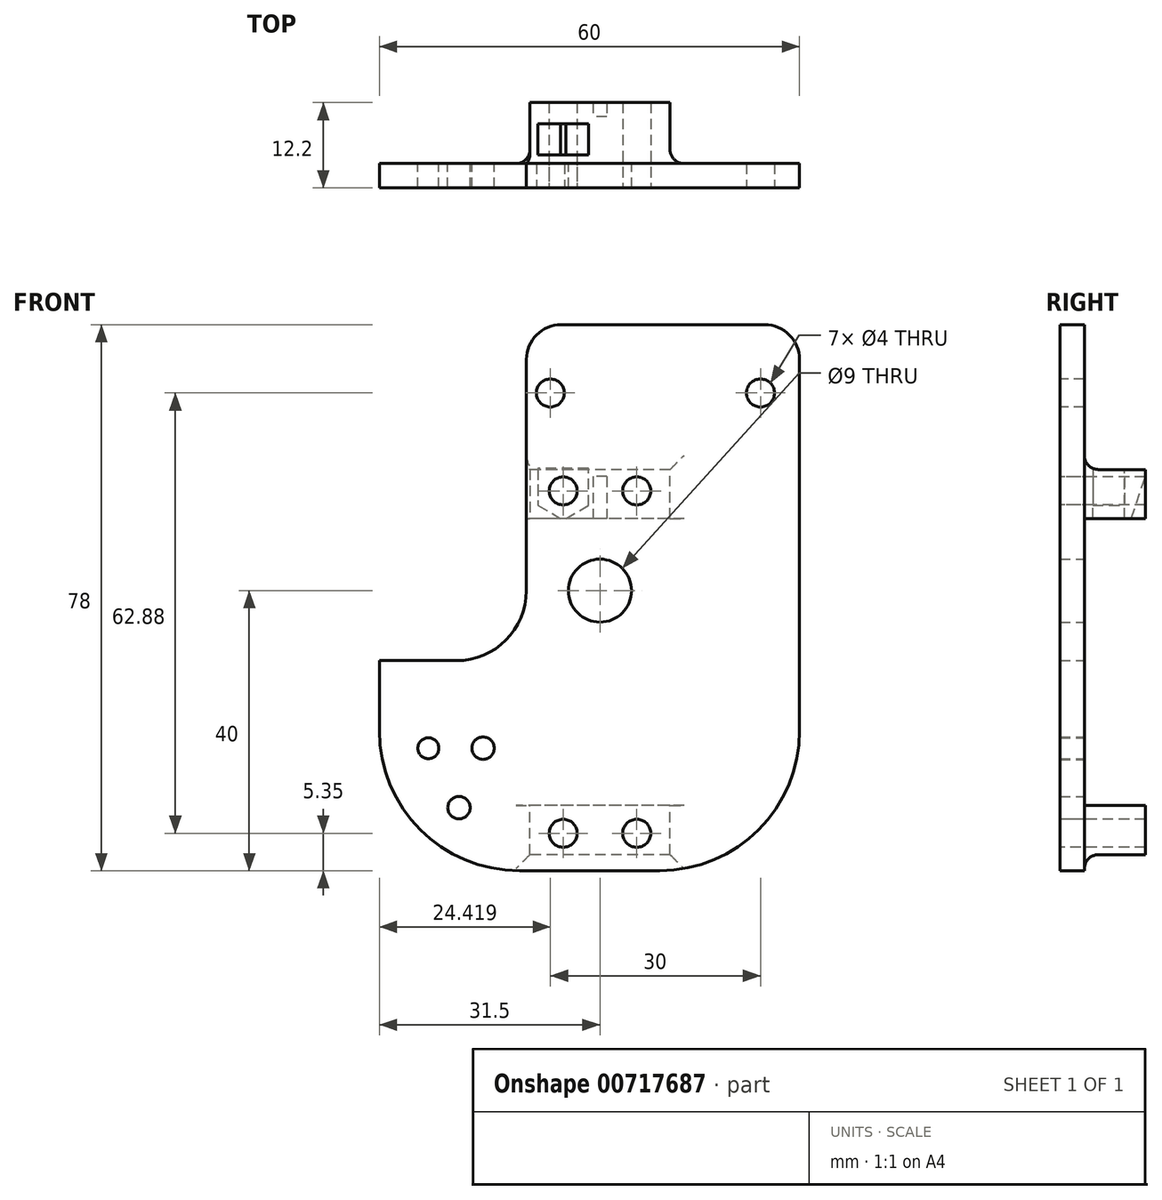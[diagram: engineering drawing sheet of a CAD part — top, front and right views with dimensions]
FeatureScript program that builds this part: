
annotation { "Feature Type Name" : "Feature", "Feature Type Description" : "" }
export const myFeature = defineFeature(function(context is Context, id is Id, definition is map)
    precondition{}
    {
        {
            var Q0;
            Q0=qCreatedBy(makeId("Front.planeOp"),FACE);
            var sketch = newSketch(context, id + "F0", { "sketchPlane" : qUnion([Q0])});
            skPoint(sketch, "E0.middle", {"position": v(0, 0) * mm});
            skLineSegment(sketch, "E1.bottom", {"start": v(-21.91, -4.91) * mm, "end": v(0.79, 17.64) * mm, "construction": true});
            skLineSegment(sketch, "E1.top", {"start": v(-25.44, -1.36) * mm, "end": v(-2.73, 21.19) * mm, "construction": true});
            skPoint(sketch, "E1.middle", {"position": v(-12.32, 8.14) * mm});
            skArc(sketch, "E2", {"start": v(-25.44, -1.36) * mm, "mid": v(-25.45, -4.9) * mm, "end": v(-21.91, -4.91) * mm, "construction": true});
            skArc(sketch, "E3", {"start": v(0.79, 17.64) * mm, "mid": v(0.8, 21.17) * mm, "end": v(-2.73, 21.19) * mm, "construction": true});
            skCircle(sketch, "E4", {"center": v(-18, 2.5) * mm, "radius": 1.5 * mm});
            skCircle(sketch, "E5", {"center": v(-10.2, 2.5) * mm, "radius": 2.5 * mm, "construction": true});
            skLineSegment(sketch, "E6", {"start": v(-21.58, -5.08) * mm, "end": v(-17.16, 26.62) * mm, "construction": true});
            skLineSegment(sketch, "E7", {"start": v(-16.63, -5.77) * mm, "end": v(-12.21, 25.92) * mm, "construction": true});
            skArc(sketch, "E8", {"start": v(-21.58, -5.08) * mm, "mid": v(-19.45, -7.9) * mm, "end": v(-16.63, -5.77) * mm, "construction": true});
            skArc(sketch, "E9", {"start": v(-12.21, 25.92) * mm, "mid": v(-14.34, 28.75) * mm, "end": v(-17.16, 26.62) * mm, "construction": true});
            skLineSegment(sketch, "E10", {"start": v(-1.22, 10.2) * mm, "end": v(9.5, 41.42) * mm, "construction": true});
            skLineSegment(sketch, "E11", {"start": v(3.5, 8.58) * mm, "end": v(14.22, 39.8) * mm, "construction": true});
            skArc(sketch, "E12", {"start": v(-1.22, 10.2) * mm, "mid": v(0.33, 7.03) * mm, "end": v(3.5, 8.58) * mm, "construction": true});
            skArc(sketch, "E13", {"start": v(14.22, 39.8) * mm, "mid": v(12.67, 42.97) * mm, "end": v(9.5, 41.42) * mm, "construction": true});
            skLineSegment(sketch, "E14", {"start": v(-19.1, -5.42) * mm, "end": v(-14.69, 26.27) * mm, "construction": true});
            skLineSegment(sketch, "E15", {"start": v(1.14, 9.4) * mm, "end": v(11.86, 40.6) * mm, "construction": true});
            skPoint(sketch, "E16", {"position": v(6.5, 25) * mm});
            skLineSegment(sketch, "E17", {"start": v(23.11, 23.42) * mm, "end": v(-9.84, 21.59) * mm, "construction": true});
            skLineSegment(sketch, "E18", {"start": v(22.84, 28.41) * mm, "end": v(-10.11, 26.58) * mm, "construction": true});
            skArc(sketch, "E19", {"start": v(23.11, 23.42) * mm, "mid": v(25.47, 26.06) * mm, "end": v(22.84, 28.41) * mm, "construction": true});
            skArc(sketch, "E20", {"start": v(-10.11, 26.58) * mm, "mid": v(-12.47, 23.94) * mm, "end": v(-9.84, 21.59) * mm, "construction": true});
            skLineSegment(sketch, "E21", {"start": v(22.97, 25.92) * mm, "end": v(-9.97, 24.08) * mm, "construction": true});
            skPoint(sketch, "E22", {"position": v(-16.9, 10.42) * mm});
            skCircle(sketch, "E23", {"center": v(6.5, 25) * mm, "radius": 4.5 * mm});
            skLineSegment(sketch, "E24.bottom", {"start": v(-25, 45) * mm, "end": v(35, 45) * mm});
            skLineSegment(sketch, "E24.top", {"start": v(-25, -15) * mm, "end": v(35, -15) * mm});
            skLineSegment(sketch, "E24.left", {"start": v(-25, 45) * mm, "end": v(-25, -15) * mm});
            skLineSegment(sketch, "E24.right", {"start": v(35, 45) * mm, "end": v(35, -15) * mm});
            skCircle(sketch, "E25", {"center": v(6.5, 25) * mm, "radius": 6 * mm, "construction": true});
            skLineSegment(sketch, "E26", {"start": v(-23.68, -3.14) * mm, "end": v(-0.97, 19.41) * mm, "construction": true});
            skCircle(sketch, "E27", {"center": v(-18, 2.5) * mm, "radius": 10.5 * mm, "construction": true});
            skPoint(sketch, "E28", {"position": v(-25.45, -4.9) * mm});
            skPoint(sketch, "E29", {"position": v(-19.45, -7.9) * mm});
            skCircle(sketch, "E30", {"center": v(-13.63, -6) * mm, "radius": 2.5 * mm, "construction": true});
            skSolve(sketch);
        }
        {
            var Q0;
            Q0=makeQuery(id+"F0.imprint","IMPRINT",FACE,{"disambiguationData":[TD([[makeQuery(id+"F0.imprint","IMPRINT",EDGE,{"derivedFrom":sQuery(id+"F0.wireOp",EDGE,"E4")}),-1.0]])]});
            extrude(context, id + "F1", {"entities" : qUnion([Q0]), "depth" : 3.5 * mm, "offsetDistance" : 25 * mm});
        }
        {
            var Q0;
            Q0=makeQuery(id+"F1.opExtrude","CAP_FACE",FACE,{"disambiguationData":[OSD([sQuery(id+"F0.wireOp",EDGE,"E4"),sQuery(id+"F0.wireOp",EDGE,"E23"),sQuery(id+"F0.wireOp",EDGE,"E24.bottom"),sQuery(id+"F0.wireOp",EDGE,"E24.top"),sQuery(id+"F0.wireOp",EDGE,"E24.left"),sQuery(id+"F0.wireOp",EDGE,"E24.right")])],"isStart":false});
            var sketch = newSketch(context, id + "F2", { "sketchPlane" : qUnion([Q0])});
            skLineSegment(sketch, "E31.bottom", {"start": v(11.75, -9.65) * mm, "end": v(1.25, -9.65) * mm, "construction": true});
            skLineSegment(sketch, "E31.top", {"start": v(11.75, 39.25) * mm, "end": v(1.25, 39.25) * mm, "construction": true});
            skLineSegment(sketch, "E31.left", {"start": v(11.75, -9.65) * mm, "end": v(11.75, 39.25) * mm, "construction": true});
            skLineSegment(sketch, "E31.right", {"start": v(1.25, -9.65) * mm, "end": v(1.25, 39.25) * mm, "construction": true});
            skPoint(sketch, "E31.middle", {"position": v(6.5, 14.8) * mm});
            skLineSegment(sketch, "E32.bottom", {"start": v(16.5, 35.3) * mm, "end": v(-3.5, 35.3) * mm});
            skLineSegment(sketch, "E32.top", {"start": v(16.5, 42.3) * mm, "end": v(-3.5, 42.3) * mm});
            skLineSegment(sketch, "E32.left", {"start": v(16.5, 35.3) * mm, "end": v(16.5, 42.3) * mm});
            skLineSegment(sketch, "E32.right", {"start": v(-3.5, 35.3) * mm, "end": v(-3.5, 42.3) * mm});
            skPoint(sketch, "E32.middle", {"position": v(6.5, 38.8) * mm});
            skLineSegment(sketch, "E33.bottom", {"start": v(16.5, -12.7) * mm, "end": v(-3.5, -12.7) * mm});
            skLineSegment(sketch, "E33.top", {"start": v(16.5, -5.7) * mm, "end": v(-3.5, -5.7) * mm});
            skLineSegment(sketch, "E33.left", {"start": v(16.5, -12.7) * mm, "end": v(16.5, -5.7) * mm});
            skLineSegment(sketch, "E33.right", {"start": v(-3.5, -12.7) * mm, "end": v(-3.5, -5.7) * mm});
            skPoint(sketch, "E33.middle", {"position": v(6.5, -9.2) * mm});
            skLineSegment(sketch, "E34", {"start": v(11.75, 14.8) * mm, "end": v(1.25, 14.8) * mm, "construction": true});
            skLineSegment(sketch, "E35", {"start": v(6.5, 39.25) * mm, "end": v(6.5, -9.65) * mm, "construction": true});
            skSolve(sketch);
        }
        {
            var Q0;
            Q0 = qSketchRegion(id + "F2", true);
            extrude(context, id + "F3", {"entities" : qUnion([Q0]), "operationType" : NewBodyOperationType.ADD, "oppositeDirection" : true, "depth" : 12.2 * mm, "offsetDistance" : 25 * mm});
        }
        {
            var Q0;
            Q0=sQuery(id+"F2.wireOp",VERTEX,"E31.left.end");
            var Q1;
            Q1=sQuery(id+"F2.wireOp",VERTEX,"E31.top.end");
            var Q2;
            Q2=sQuery(id+"F2.wireOp",VERTEX,"E31.left.start");
            var Q3;
            Q3=sQuery(id+"F2.wireOp",VERTEX,"E31.right.start");
            var Q4;
            Q4=makeQuery(id+"F1.opExtrude","SWEPT_BODY",BODY,{"disambiguationData":[OSD([sQuery(id+"F0.wireOp",EDGE,"E4"),sQuery(id+"F0.wireOp",EDGE,"E23"),sQuery(id+"F0.wireOp",EDGE,"E24.bottom"),sQuery(id+"F0.wireOp",EDGE,"E24.top"),sQuery(id+"F0.wireOp",EDGE,"E24.left"),sQuery(id+"F0.wireOp",EDGE,"E24.right")])]});
            hole(context, id + "F4", {"style" : HoleStyle.SIMPLE, "endStyle" : HoleEndStyle.THROUGH, "holeDiameter" : 4 * mm, "majorDiameter" : 5 * mm, "isTappedThrough" : true, "tappedDepth" : 2.3 * mm, "tapClearance" : 3, "startFromSketch" : true, "locations" : qUnion([Q0, Q1, Q2, Q3]), "scope" : qUnion([Q4])});
        }
        {
            var Q0;
            Q0=makeQuery(id+"F3.opExtrude","CAP_FACE",FACE,{"disambiguationData":[OSD([sQuery(id+"F2.wireOp",EDGE,"E32.bottom"),sQuery(id+"F2.wireOp",EDGE,"E32.top"),sQuery(id+"F2.wireOp",EDGE,"E32.left"),sQuery(id+"F2.wireOp",EDGE,"E32.right")])],"isStart":false});
            cPlane(context, id + "F5", {"entities" : qUnion([Q0]), "cplaneType" : CPlaneType.OFFSET, "offset" : 3 * mm, "oppositeDirection" : true, "width" : 150 * mm, "height" : 150 * mm});
        }
        {
            var Q0;
            Q0=sQuery(id+"F2.wireOp",EDGE,"E35");
            cPoint(context, id + "F6", {"entities" : qUnion([Q0]), "parameter" : 0.5});
        }
        {
            var Q0;
            Q0=qCreatedBy(makeId("Top.planeOp"),FACE);
            var Q1;
            Q1 = qCreatedBy(id + "F6" ,VERTEX);
            cPlane(context, id + "F7", {"entities" : qUnion([Q0, Q1]), "cplaneType" : CPlaneType.PLANE_POINT, "offset" : 25 * mm, "width" : 150 * mm, "height" : 150 * mm});
        }
        {
            var Q0;
            Q0=qCreatedBy(makeId("Right.planeOp"),FACE);
            var Q1;
            Q1=sQuery(id+"F0.wireOp",VERTEX,"E16");
            cPlane(context, id + "F8", {"entities" : qUnion([Q0, Q1]), "cplaneType" : CPlaneType.PLANE_POINT, "offset" : 25 * mm, "width" : 150 * mm, "height" : 150 * mm});
        }
        {
            var Q0;
            Q0=qCreatedBy(id+"F5.planeOp",FACE);
            var sketch = newSketch(context, id + "F9", { "sketchPlane" : qUnion([Q0])});
            skCircle(sketch, "E36.cCircle", {"center": v(-1.25, 39.25) * mm, "radius": 3.6 * mm, "construction": true});
            skLineSegment(sketch, "E36.0", {"start": v(2.35, 37.17) * mm, "end": v(-1.25, 35.1) * mm});
            skLineSegment(sketch, "E36.1", {"start": v(-1.25, 35.1) * mm, "end": v(-4.85, 37.17) * mm});
            skLineSegment(sketch, "E36.2", {"start": v(-4.85, 37.17) * mm, "end": v(-4.85, 41.33) * mm});
            skLineSegment(sketch, "E36.3", {"start": v(-4.85, 41.33) * mm, "end": v(-1.25, 43.4) * mm});
            skLineSegment(sketch, "E36.4", {"start": v(-1.25, 43.4) * mm, "end": v(2.35, 41.33) * mm});
            skLineSegment(sketch, "E36.5", {"start": v(2.35, 41.33) * mm, "end": v(2.35, 37.17) * mm});
            skPoint(sketch, "E36.0.midPoint", {"position": v(0.55, 36.13) * mm});
            skLineSegment(sketch, "E37", {"start": v(-4.85, 41.33) * mm, "end": v(-4.85, 42.3) * mm});
            skLineSegment(sketch, "E38", {"start": v(-4.85, 42.3) * mm, "end": v(2.35, 42.3) * mm});
            skLineSegment(sketch, "E39", {"start": v(2.35, 42.3) * mm, "end": v(2.35, 41.33) * mm});
            skSolve(sketch);
        }
        {
            var Q0;
            Q0 = qSketchRegion(id + "F9", true);
            extrude(context, id + "F10", {"entities" : qUnion([Q0]), "operationType" : NewBodyOperationType.REMOVE, "oppositeDirection" : true, "depth" : 4.5 * mm, "offsetDistance" : 25 * mm});
        }
        {
            var Q0;
            Q0=qCreatedBy(makeId("Front.planeOp"),FACE);
            var sketch = newSketch(context, id + "F11", { "sketchPlane" : qUnion([Q0])});
            skLineSegment(sketch, "E40.bottom", {"start": v(35, 45) * mm, "end": v(-4, 45) * mm});
            skLineSegment(sketch, "E40.top", {"start": v(35, 63) * mm, "end": v(-4, 63) * mm});
            skLineSegment(sketch, "E40.left", {"start": v(35, 45) * mm, "end": v(35, 63) * mm});
            skLineSegment(sketch, "E40.right", {"start": v(-4, 45) * mm, "end": v(-4, 63) * mm});
            skSolve(sketch);
        }
        {
            var Q0;
            Q0=makeQuery(id+"F11.imprint","IMPRINT",FACE,{"disambiguationData":[TD([[makeQuery(id+"F11.imprint","IMPRINT",EDGE,{"derivedFrom":sQuery(id+"F11.wireOp",EDGE,"E40.bottom")}),-1.0]])]});
            var Q1;
            Q1=makeQuery(id+"F1.opExtrude","CAP_FACE",FACE,{"disambiguationData":[OSD([sQuery(id+"F0.wireOp",EDGE,"E4"),sQuery(id+"F0.wireOp",EDGE,"E23"),sQuery(id+"F0.wireOp",EDGE,"E24.bottom"),sQuery(id+"F0.wireOp",EDGE,"E24.top"),sQuery(id+"F0.wireOp",EDGE,"E24.left"),sQuery(id+"F0.wireOp",EDGE,"E24.right")])],"isStart":false});
            extrude(context, id + "F12", {"entities" : qUnion([Q0]), "operationType" : NewBodyOperationType.ADD, "endBound" : BoundingType.UP_TO_SURFACE, "depth" : 25 * mm, "endBoundEntityFace" : qUnion([Q1]), "offsetDistance" : 25 * mm});
        }
        {
            var Q0;
            Q0=makeQuery(id+"F2.imprint","IMPRINT",FACE,{"disambiguationData":[TD([[makeQuery(id+"F2.imprint","IMPRINT",EDGE,{"derivedFrom":sQuery(id+"F2.wireOp",EDGE,"E32.bottom")}),1.0]])]});
            var sketch = newSketch(context, id + "F13", { "sketchPlane" : qUnion([Q0])});
            skPoint(sketch, "E41", {"position": v(-0.58, 53.23) * mm});
            skPoint(sketch, "E42", {"position": v(29.42, 53.23) * mm});
            skLineSegment(sketch, "E43", {"start": v(-32.58, 62.23) * mm, "end": v(-32.58, -14.27) * mm, "construction": true});
            skLineSegment(sketch, "E44", {"start": v(-32.58, -9.27) * mm, "end": v(-22.58, -9.27) * mm, "construction": true});
            skCircle(sketch, "E45", {"center": v(-25.58, -9.27) * mm, "radius": 3 * mm, "construction": true});
            skLineSegment(sketch, "E46", {"start": v(-95.3, 32.33) * mm, "end": v(-95.3, -44.17) * mm, "construction": true});
            skLineSegment(sketch, "E47", {"start": v(-95.3, -39.17) * mm, "end": v(-85.3, -39.17) * mm, "construction": true});
            skLineSegment(sketch, "E48", {"start": v(-151.09, 43.62) * mm, "end": v(-151.09, -32.88) * mm, "construction": true});
            skLineSegment(sketch, "E49", {"start": v(-151.09, -27.88) * mm, "end": v(-141.09, -27.88) * mm, "construction": true});
            skLineSegment(sketch, "E50", {"start": v(-178.62, 52.62) * mm, "end": v(-178.62, -23.88) * mm, "construction": true});
            skLineSegment(sketch, "E51", {"start": v(-178.62, -18.88) * mm, "end": v(-168.62, -18.88) * mm, "construction": true});
            skSolve(sketch);
        }
        {
            var Q0;
            Q0=sQuery(id+"F13.wireOp",VERTEX,"E41");
            var Q1;
            Q1=sQuery(id+"F13.wireOp",VERTEX,"E42");
            var Q2;
            Q2=makeQuery(id+"F1.opExtrude","SWEPT_BODY",BODY,{"disambiguationData":[OSD([sQuery(id+"F0.wireOp",EDGE,"E4"),sQuery(id+"F0.wireOp",EDGE,"E23"),sQuery(id+"F0.wireOp",EDGE,"E24.bottom"),sQuery(id+"F0.wireOp",EDGE,"E24.top"),sQuery(id+"F0.wireOp",EDGE,"E24.left"),sQuery(id+"F0.wireOp",EDGE,"E24.right")])]});
            hole(context, id + "F14", {"style" : HoleStyle.SIMPLE, "endStyle" : HoleEndStyle.THROUGH, "holeDiameter" : 4 * mm, "majorDiameter" : 5 * mm, "isTappedThrough" : true, "tappedDepth" : 2.3 * mm, "tapClearance" : 3, "startFromSketch" : true, "locations" : qUnion([Q0, Q1]), "scope" : qUnion([Q2])});
        }
        {
            var Q0;
            Q0=sQuery(id+"F0.wireOp",VERTEX,"E5.center");
            var Q1;
            Q1=sQuery(id+"F0.wireOp",VERTEX,"E30.center");
            var Q2;
            Q2=makeQuery(id+"F1.opExtrude","SWEPT_BODY",BODY,{"disambiguationData":[OSD([sQuery(id+"F0.wireOp",EDGE,"E4"),sQuery(id+"F0.wireOp",EDGE,"E23"),sQuery(id+"F0.wireOp",EDGE,"E24.bottom"),sQuery(id+"F0.wireOp",EDGE,"E24.top"),sQuery(id+"F0.wireOp",EDGE,"E24.left"),sQuery(id+"F0.wireOp",EDGE,"E24.right")])]});
            hole(context, id + "F15", {"style" : HoleStyle.SIMPLE, "endStyle" : HoleEndStyle.THROUGH, "oppositeDirection" : true, "holeDiameter" : 3.2 * mm, "majorDiameter" : 5 * mm, "isTappedThrough" : true, "tappedDepth" : 2.3 * mm, "tapClearance" : 3, "startFromSketch" : true, "locations" : qUnion([Q0, Q1]), "scope" : qUnion([Q2])});
        }
        {
            var Q0;
            Q0=qCreatedBy(makeId("Front.planeOp"),FACE);
            var sketch = newSketch(context, id + "F16", { "sketchPlane" : qUnion([Q0])});
            skLineSegment(sketch, "E52.bottom", {"start": v(-25, 45) * mm, "end": v(-4, 45) * mm});
            skLineSegment(sketch, "E52.top", {"start": v(-25, 15) * mm, "end": v(-4, 15) * mm});
            skLineSegment(sketch, "E52.left", {"start": v(-25, 45) * mm, "end": v(-25, 15) * mm});
            skLineSegment(sketch, "E52.right", {"start": v(-4, 45) * mm, "end": v(-4, 15) * mm});
            skSolve(sketch);
        }
        {
            var Q0;
            Q0=makeQuery(id+"F16.imprint","IMPRINT",FACE,{"disambiguationData":[TD([[makeQuery(id+"F16.imprint","IMPRINT",EDGE,{"derivedFrom":sQuery(id+"F16.wireOp",EDGE,"E52.bottom")}),-1.0]])]});
            extrude(context, id + "F17", {"entities" : qUnion([Q0]), "operationType" : NewBodyOperationType.REMOVE, "depth" : 25 * mm, "offsetDistance" : 25 * mm});
        }
        {
            var Q0;
            Q0=makeQuery(id+"F1.opExtrude","SWEPT_EDGE",EDGE,{"disambiguationData":[OSD([sQuery(id+"F0.wireOp",EDGE,"E24.top"),sQuery(id+"F0.wireOp",EDGE,"E24.right")])]});
            var Q1;
            Q1=makeQuery(id+"F1.opExtrude","SWEPT_EDGE",EDGE,{"disambiguationData":[OSD([sQuery(id+"F0.wireOp",EDGE,"E24.top"),sQuery(id+"F0.wireOp",EDGE,"E24.left")])]});
            fillet(context, id + "F18", {"entities" : qUnion([Q0, Q1]), "radius" : 20 * mm, "tangentPropagation" : true, "allowEdgeOverflow" : false});
        }
        {
            var Q0;
            Q0=makeQuery(id+"F12.opExtrude","SWEPT_EDGE",EDGE,{"disambiguationData":[OSD([sQuery(id+"F11.wireOp",EDGE,"E40.bottom"),sQuery(id+"F11.wireOp",EDGE,"E40.right")])]});
            var Q1;
            Q1=makeQuery(id+"F12.opExtrude","SWEPT_EDGE",EDGE,{"disambiguationData":[OSD([sQuery(id+"F11.wireOp",EDGE,"E40.top"),sQuery(id+"F11.wireOp",EDGE,"E40.right")])]});
            var Q2;
            Q2=makeQuery(id+"F12.opExtrude","SWEPT_EDGE",EDGE,{"disambiguationData":[OSD([sQuery(id+"F11.wireOp",EDGE,"E40.top"),sQuery(id+"F11.wireOp",EDGE,"E40.left")])]});
            fillet(context, id + "F19", {"entities" : qUnion([Q0, Q1, Q2]), "radius" : 5 * mm, "tangentPropagation" : true, "allowEdgeOverflow" : false});
        }
        {
            var Q0;
            Q0=makeQuery(id+"F17.boolean.opBoolean","COPY",EDGE,{"derivedFrom":makeQuery(id+"F17.opExtrude","SWEPT_EDGE",EDGE,{"disambiguationData":[OSD([sQuery(id+"F16.wireOp",EDGE,"E52.top"),sQuery(id+"F16.wireOp",EDGE,"E52.left")])]})});
            var Q1;
            Q1=makeQuery(id+"F17.boolean.opBoolean","COPY",EDGE,{"derivedFrom":makeQuery(id+"F17.opExtrude","SWEPT_EDGE",EDGE,{"disambiguationData":[OSD([sQuery(id+"F16.wireOp",EDGE,"E52.top"),sQuery(id+"F16.wireOp",EDGE,"E52.right")])]})});
            fillet(context, id + "F20", {"entities" : qUnion([Q0, Q1]), "radius" : 10 * mm, "tangentPropagation" : true, "allowEdgeOverflow" : false});
        }
        {
            var Q0;
            Q0=makeQuery(id+"F3.boolean.opBoolean","INTERSECT",EDGE,{"derivedFrom":[makeQuery(id+"F1.opExtrude","CAP_FACE",FACE,{"disambiguationData":[OSD([sQuery(id+"F0.wireOp",EDGE,"E4"),sQuery(id+"F0.wireOp",EDGE,"E23"),sQuery(id+"F0.wireOp",EDGE,"E24.bottom"),sQuery(id+"F0.wireOp",EDGE,"E24.top"),sQuery(id+"F0.wireOp",EDGE,"E24.left"),sQuery(id+"F0.wireOp",EDGE,"E24.right")])],"isStart":true}),makeQuery(id+"F3.opExtrude","SWEPT_FACE",FACE,{"disambiguationData":[OSD([sQuery(id+"F2.wireOp",EDGE,"E33.bottom")])]})]});
            var Q1;
            Q1=makeQuery(id+"F3.boolean.opBoolean","INTERSECT",EDGE,{"derivedFrom":[makeQuery(id+"F1.opExtrude","CAP_FACE",FACE,{"disambiguationData":[OSD([sQuery(id+"F0.wireOp",EDGE,"E4"),sQuery(id+"F0.wireOp",EDGE,"E23"),sQuery(id+"F0.wireOp",EDGE,"E24.bottom"),sQuery(id+"F0.wireOp",EDGE,"E24.top"),sQuery(id+"F0.wireOp",EDGE,"E24.left"),sQuery(id+"F0.wireOp",EDGE,"E24.right")])],"isStart":true}),makeQuery(id+"F3.opExtrude","SWEPT_FACE",FACE,{"disambiguationData":[OSD([sQuery(id+"F2.wireOp",EDGE,"E33.left")])]})]});
            var Q2;
            Q2=makeQuery(id+"F3.boolean.opBoolean","INTERSECT",EDGE,{"derivedFrom":[makeQuery(id+"F1.opExtrude","CAP_FACE",FACE,{"disambiguationData":[OSD([sQuery(id+"F0.wireOp",EDGE,"E4"),sQuery(id+"F0.wireOp",EDGE,"E23"),sQuery(id+"F0.wireOp",EDGE,"E24.bottom"),sQuery(id+"F0.wireOp",EDGE,"E24.top"),sQuery(id+"F0.wireOp",EDGE,"E24.left"),sQuery(id+"F0.wireOp",EDGE,"E24.right")])],"isStart":true}),makeQuery(id+"F3.opExtrude","SWEPT_FACE",FACE,{"disambiguationData":[OSD([sQuery(id+"F2.wireOp",EDGE,"E33.right")])]})]});
            var Q3;
            Q3=makeQuery(id+"F3.boolean.opBoolean","INTERSECT",EDGE,{"derivedFrom":[makeQuery(id+"F1.opExtrude","CAP_FACE",FACE,{"disambiguationData":[OSD([sQuery(id+"F0.wireOp",EDGE,"E4"),sQuery(id+"F0.wireOp",EDGE,"E23"),sQuery(id+"F0.wireOp",EDGE,"E24.bottom"),sQuery(id+"F0.wireOp",EDGE,"E24.top"),sQuery(id+"F0.wireOp",EDGE,"E24.left"),sQuery(id+"F0.wireOp",EDGE,"E24.right")])],"isStart":true}),makeQuery(id+"F3.opExtrude","SWEPT_FACE",FACE,{"disambiguationData":[OSD([sQuery(id+"F2.wireOp",EDGE,"E32.right")])]})]});
            var Q4;
            Q4=makeQuery(id+"F3.boolean.opBoolean","INTERSECT",EDGE,{"derivedFrom":[makeQuery(id+"F1.opExtrude","CAP_FACE",FACE,{"disambiguationData":[OSD([sQuery(id+"F0.wireOp",EDGE,"E4"),sQuery(id+"F0.wireOp",EDGE,"E23"),sQuery(id+"F0.wireOp",EDGE,"E24.bottom"),sQuery(id+"F0.wireOp",EDGE,"E24.top"),sQuery(id+"F0.wireOp",EDGE,"E24.left"),sQuery(id+"F0.wireOp",EDGE,"E24.right")])],"isStart":true}),makeQuery(id+"F3.opExtrude","SWEPT_FACE",FACE,{"disambiguationData":[OSD([sQuery(id+"F2.wireOp",EDGE,"E32.top")])]})]});
            var Q5;
            Q5=makeQuery(id+"F3.boolean.opBoolean","INTERSECT",EDGE,{"derivedFrom":[makeQuery(id+"F1.opExtrude","CAP_FACE",FACE,{"disambiguationData":[OSD([sQuery(id+"F0.wireOp",EDGE,"E4"),sQuery(id+"F0.wireOp",EDGE,"E23"),sQuery(id+"F0.wireOp",EDGE,"E24.bottom"),sQuery(id+"F0.wireOp",EDGE,"E24.top"),sQuery(id+"F0.wireOp",EDGE,"E24.left"),sQuery(id+"F0.wireOp",EDGE,"E24.right")])],"isStart":true}),makeQuery(id+"F3.opExtrude","SWEPT_FACE",FACE,{"disambiguationData":[OSD([sQuery(id+"F2.wireOp",EDGE,"E32.left")])]})]});
            fillet(context, id + "F21", {"entities" : qUnion([Q0, Q1, Q2, Q3, Q4, Q5]), "radius" : 2 * mm, "tangentPropagation" : true, "allowEdgeOverflow" : false});
        }
        {
            var Q0;
            Q0=qCreatedBy(id+"F8.planeOp",FACE);
            var sketch = newSketch(context, id + "F22", { "sketchPlane" : qUnion([Q0])});
            skLineSegment(sketch, "E53", {"start": v(8.7, 41.3) * mm, "end": v(8.7, 35.3) * mm});
            skLineSegment(sketch, "E54", {"start": v(8.7, 35.3) * mm, "end": v(6.7, 35.3) * mm});
            skLineSegment(sketch, "E55", {"start": v(6.7, 35.3) * mm, "end": v(8.7, 41.3) * mm});
            skSolve(sketch);
        }
        {
            var Q0;
            Q0=makeQuery(id+"F22.imprint","IMPRINT",FACE,{"disambiguationData":[TD([[makeQuery(id+"F22.imprint","IMPRINT",EDGE,{"derivedFrom":sQuery(id+"F22.wireOp",EDGE,"E53")}),-1.0]])]});
            extrude(context, id + "F23", {"entities" : qUnion([Q0]), "operationType" : NewBodyOperationType.REMOVE, "endBound" : BoundingType.SYMMETRIC, "depth" : 2 * mm, "offsetDistance" : 25 * mm});
        }
    });
